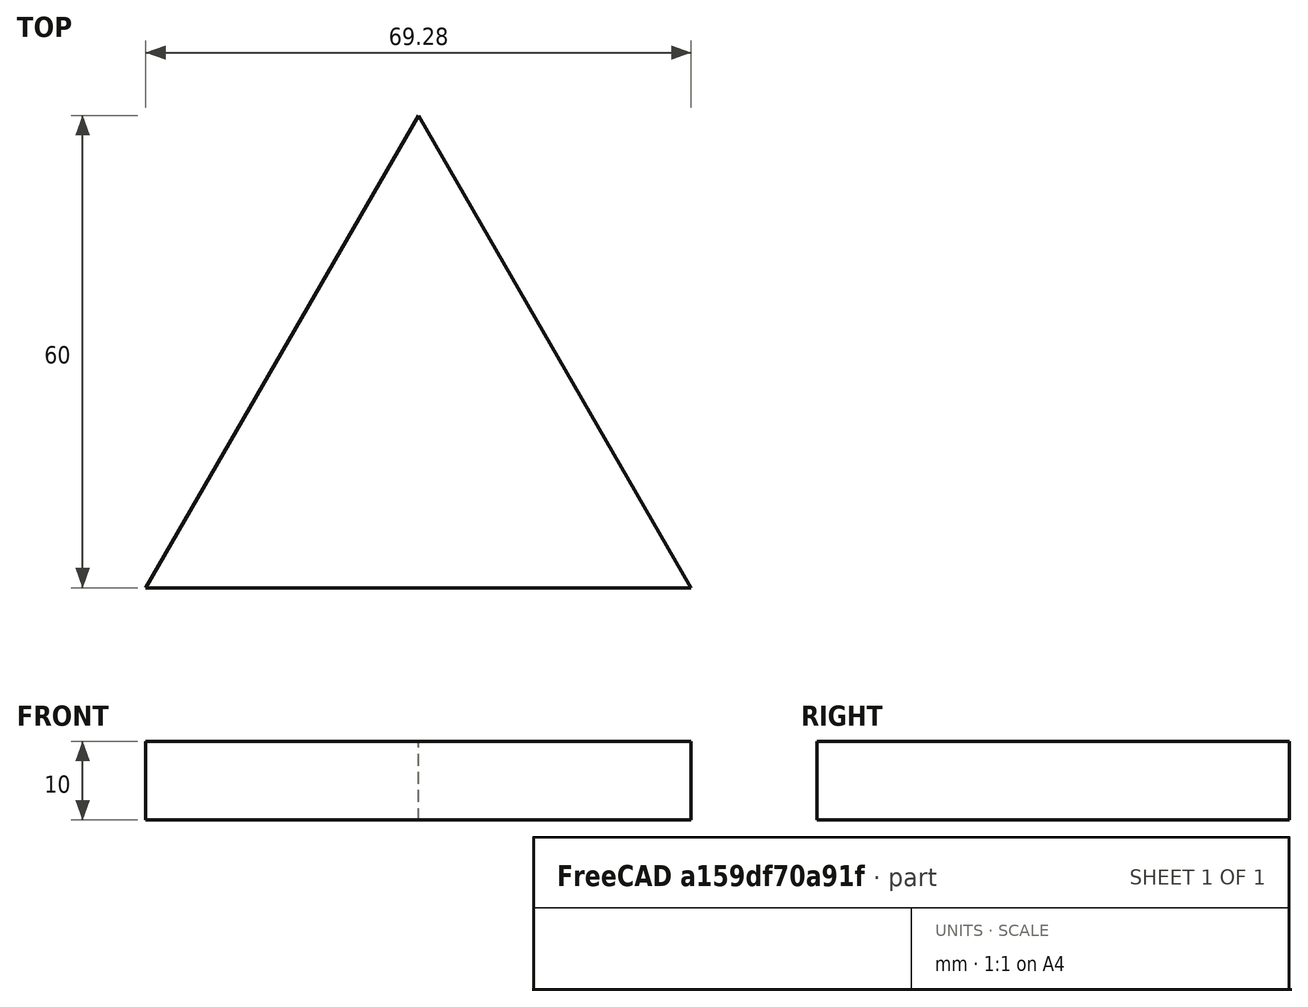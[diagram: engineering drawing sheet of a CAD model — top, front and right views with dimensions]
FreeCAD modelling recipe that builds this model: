
FCSTD DOCUMENT  (FreeCAD 0.21R33694 (Git))
Label: OJT1_T20P01_triangle
License: All rights reserved
LicenseURL: https://en.wikipedia.org/wiki/All_rights_reserved
objects: Sketcher::SketchObject×1, PartDesign::Pad×1, PartDesign::Body×1
note: 4 computed .brp shape members not serialized (recipe doc carries the construction recipe); baked Part::Feature solids carry a one-line shape summary decoded from their .brp

FEATURE [Sketcher::SketchObject] Sketch
  FullyConstrained = true
  MapMode = 5
  Support = -> [XY_Plane]
  sketch-geometry (4):
    g0: LineSegment StartX=0 StartY=30 StartZ=0 EndX=-34.641 EndY=-30 EndZ=0
    g1: LineSegment StartX=-34.641 StartY=-30 StartZ=0 EndX=34.641 EndY=-30 EndZ=0
    g2: LineSegment StartX=34.641 StartY=-30 StartZ=0 EndX=0 EndY=30 EndZ=0
    g3: LineSegment StartX=0 StartY=30 StartZ=0 EndX=0 EndY=-30 EndZ=0
  constraints (10):
    c: Coincident(g0,g1)
    c: Coincident(g1,g2)
    c: Coincident(g2,g0)
    c: PointOnObject(g3,g1)
    c: Coincident(g0,g3)
    c: Symmetric(g0,g1,g3)
    c: Symmetric(g0,g3,g-1)
    c: PointOnObject(g0,g-2)
    c: Angle(g1,g0) = 1.0472
    c: DistanceY(g3,g3) = 60
FEATURE [PartDesign::Pad] Pad
  Direction = (0,0,1)
  Length = 10
  Length2 = 10
  Profile = -> Sketch
  ReferenceAxis = -> Sketch [N_Axis]
  Type = 0
FEATURE [PartDesign::Body] Body
  Group = -> [Sketch,Pad]
  Origin = -> Origin
  Tip = -> Pad
